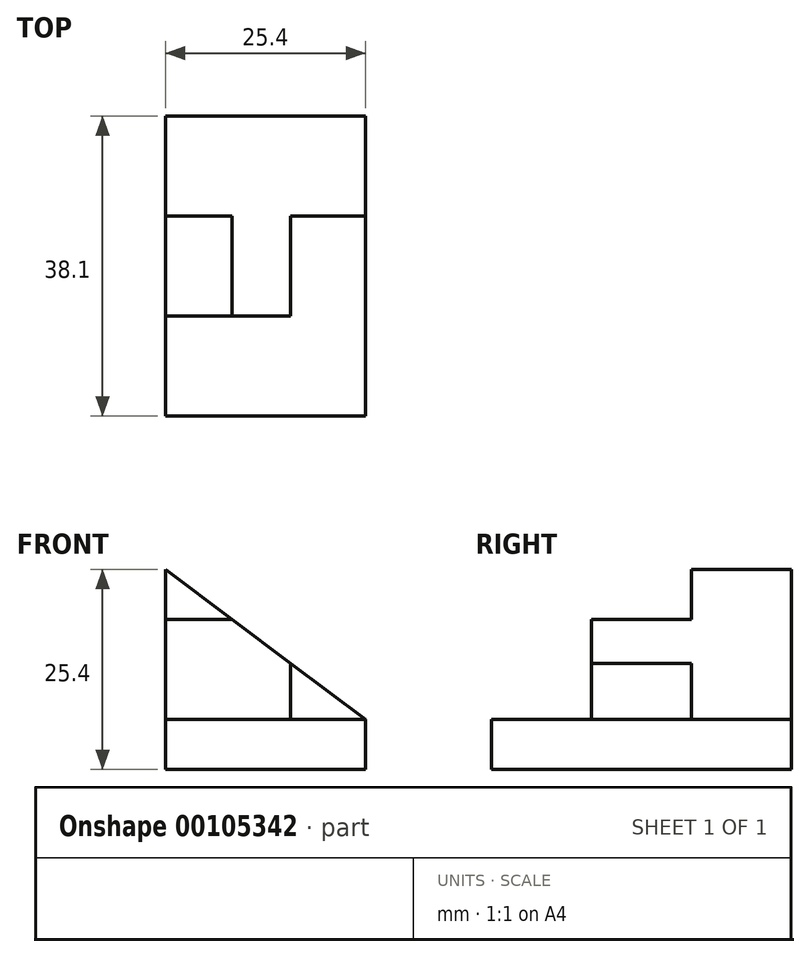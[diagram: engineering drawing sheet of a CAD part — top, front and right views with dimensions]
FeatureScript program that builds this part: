
annotation { "Feature Type Name" : "Feature", "Feature Type Description" : "" }
export const myFeature = defineFeature(function(context is Context, id is Id, definition is map)
    precondition{}
    {
        {
            var Q0;
            Q0=qCreatedBy(makeId("Front.planeOp"),FACE);
            var sketch = newSketch(context, id + "F0", { "sketchPlane" : qUnion([Q0])});
            skLineSegment(sketch, "E0.bottom", {"start": v(0, 0) * mm, "end": v(25.4, 0) * mm});
            skLineSegment(sketch, "E0.top", {"start": v(0, 6.35) * mm, "end": v(25.4, 6.35) * mm});
            skLineSegment(sketch, "E0.left", {"start": v(0, 0) * mm, "end": v(0, 6.35) * mm});
            skLineSegment(sketch, "E0.right", {"start": v(25.4, 0) * mm, "end": v(25.4, 6.35) * mm});
            skSolve(sketch);
        }
        {
            var Q0;
            Q0 = qSketchRegion(id + "F0", true);
            extrude(context, id + "F1", {"entities" : qUnion([Q0]), "endBound" : BoundingType.SYMMETRIC, "depth" : 38.1 * mm});
        }
        {
            var Q0;
            Q0=qCreatedBy(makeId("Front.planeOp"),FACE);
            var sketch = newSketch(context, id + "F2", { "sketchPlane" : qUnion([Q0])});
            skLineSegment(sketch, "E1.bottom", {"start": v(0, 6.35) * mm, "end": v(25.4, 6.35) * mm});
            skLineSegment(sketch, "E1.top", {"start": v(0, 25.4) * mm, "end": v(25.4, 25.4) * mm});
            skLineSegment(sketch, "E1.left", {"start": v(0, 6.35) * mm, "end": v(0, 25.4) * mm});
            skLineSegment(sketch, "E1.right", {"start": v(25.4, 6.35) * mm, "end": v(25.4, 25.4) * mm});
            skSolve(sketch);
        }
        {
            var Q0;
            Q0 = qSketchRegion(id + "F2", true);
            extrude(context, id + "F3", {"entities" : qUnion([Q0]), "operationType" : NewBodyOperationType.ADD, "oppositeDirection" : true, "depth" : 19.05 * mm, "hasSecondDirection" : true, "secondDirectionOppositeDirection" : false, "secondDirectionDepth" : 6.35 * mm});
        }
        {
            var Q0;
            Q0=qCreatedBy(makeId("Front.planeOp"),FACE);
            var sketch = newSketch(context, id + "F4", { "sketchPlane" : qUnion([Q0])});
            skLineSegment(sketch, "E2", {"start": v(0, 25.4) * mm, "end": v(25.4, 6.35) * mm});
            skLineSegment(sketch, "E3", {"start": v(25.4, 6.35) * mm, "end": v(25.4, 25.4) * mm});
            skLineSegment(sketch, "E4", {"start": v(25.4, 25.4) * mm, "end": v(0, 25.4) * mm});
            skSolve(sketch);
        }
        {
            var Q0;
            Q0 = qSketchRegion(id + "F4", true);
            extrude(context, id + "F5", {"entities" : qUnion([Q0]), "operationType" : NewBodyOperationType.REMOVE, "endBound" : BoundingType.SYMMETRIC, "oppositeDirection" : true, "depth" : 127 * mm});
        }
        {
            var Q0;
            Q0=qCreatedBy(makeId("Front.planeOp"),FACE);
            var sketch = newSketch(context, id + "F6", { "sketchPlane" : qUnion([Q0])});
            skLineSegment(sketch, "E5", {"start": v(0, 19.05) * mm, "end": v(8.47, 19.05) * mm});
            skLineSegment(sketch, "E6", {"start": v(8.47, 19.05) * mm, "end": v(0, 25.4) * mm});
            skLineSegment(sketch, "E7", {"start": v(0, 25.4) * mm, "end": v(0, 19.05) * mm});
            skSolve(sketch);
        }
        {
            var Q0;
            Q0 = qSketchRegion(id + "F6", true);
            extrude(context, id + "F7", {"entities" : qUnion([Q0]), "operationType" : NewBodyOperationType.REMOVE, "depth" : 25.4 * mm, "hasSecondDirection" : true, "secondDirectionOppositeDirection" : true, "secondDirectionDepth" : 6.35 * mm});
        }
        {
            var Q0;
            Q0=qCreatedBy(makeId("Front.planeOp"),FACE);
            var sketch = newSketch(context, id + "F8", { "sketchPlane" : qUnion([Q0])});
            skLineSegment(sketch, "E8", {"start": v(15.88, 6.35) * mm, "end": v(15.88, 13.5) * mm});
            skLineSegment(sketch, "E9", {"start": v(25.4, 6.35) * mm, "end": v(15.88, 6.35) * mm});
            skLineSegment(sketch, "E10", {"start": v(15.88, 13.5) * mm, "end": v(25.4, 6.35) * mm});
            skSolve(sketch);
        }
        {
            var Q0;
            Q0 = qSketchRegion(id + "F8", true);
            extrude(context, id + "F9", {"entities" : qUnion([Q0]), "operationType" : NewBodyOperationType.REMOVE, "depth" : 25.4 * mm, "hasSecondDirection" : true, "secondDirectionOppositeDirection" : true, "secondDirectionDepth" : 6.35 * mm});
        }
    });
